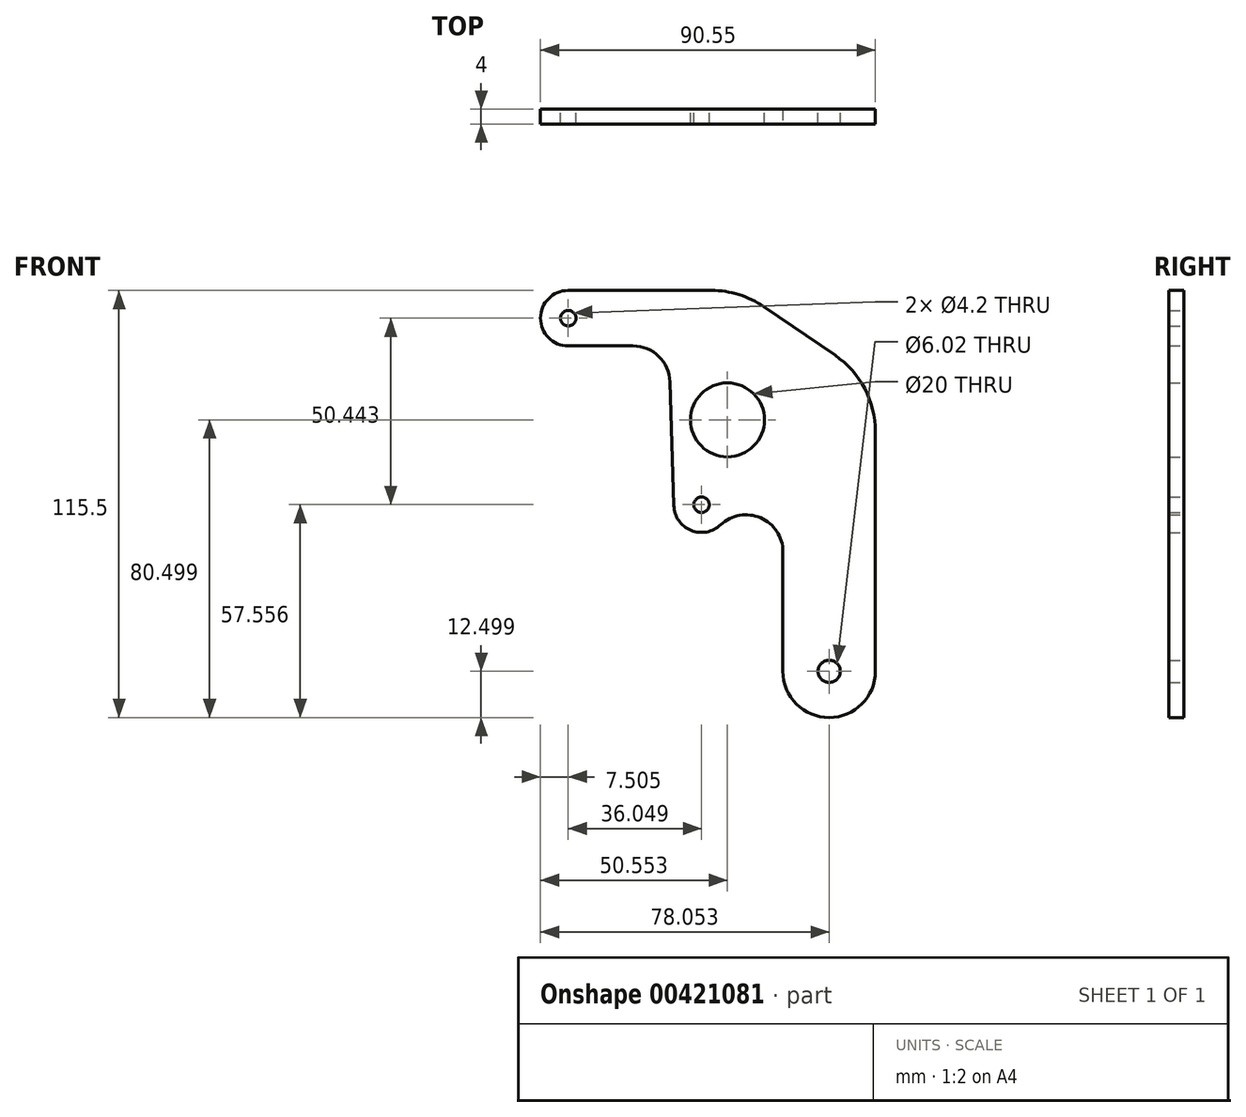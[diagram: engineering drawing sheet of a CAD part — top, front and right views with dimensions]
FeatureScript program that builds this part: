
annotation { "Feature Type Name" : "Feature", "Feature Type Description" : "" }
export const myFeature = defineFeature(function(context is Context, id is Id, definition is map)
    precondition{}
    {
        {
            var Q0;
            Q0=qCreatedBy(makeId("Front.planeOp"),FACE);
            var sketch = newSketch(context, id + "F0", { "sketchPlane" : qUnion([Q0])});
            skLineSegment(sketch, "E0", {"start": v(17.8, -32.82) * mm, "end": v(17.8, 31.99) * mm});
            skLineSegment(sketch, "E1", {"start": v(6.91, 52.62) * mm, "end": v(-12.39, 65.82) * mm});
            skLineSegment(sketch, "E2", {"start": v(-26.5, 70.18) * mm, "end": v(-65.25, 70.18) * mm});
            skLineSegment(sketch, "E3", {"start": v(-65.25, 55.18) * mm, "end": v(-47.72, 55.18) * mm});
            skLineSegment(sketch, "E4", {"start": v(-7.2, 25.92) * mm, "end": v(-7.2, -32.82) * mm});
            skLineSegment(sketch, "E5", {"start": v(-23.76, 7.07) * mm, "end": v(-6.5, 25.25) * mm});
            skLineSegment(sketch, "E6.trimOffspring", {"start": v(-7.2, 25.92) * mm, "end": v(-6.5, 25.25) * mm});
            skCircle(sketch, "E7", {"center": v(-29.2, 12.24) * mm, "radius": 2.1 * mm});
            skCircle(sketch, "E8", {"center": v(-65.25, 62.68) * mm, "radius": 2.1 * mm});
            skCircle(sketch, "E9", {"center": v(5.3, -32.82) * mm, "radius": 3.01 * mm});
            skCircle(sketch, "E10", {"center": v(-22.2, 35.18) * mm, "radius": 10 * mm});
            skArc(sketch, "E11", {"start": v(-36.7, 12) * mm, "mid": v(-31.87, 5.23) * mm, "end": v(-23.76, 7.07) * mm});
            skArc(sketch, "E12", {"start": v(-65.25, 70.18) * mm, "mid": v(-72.75, 62.68) * mm, "end": v(-65.25, 55.18) * mm});
            skArc(sketch, "E13", {"start": v(-7.2, -32.82) * mm, "mid": v(5.3, -45.32) * mm, "end": v(17.8, -32.82) * mm});
            skLineSegment(sketch, "E14.trimOffspring", {"start": v(-27.67, 4.9) * mm, "end": v(-26.47, 4.21) * mm});
            skPoint(sketch, "E15.orphan", {"position": v(17.8, -42.82) * mm});
            skPoint(sketch, "E16.orphan", {"position": v(-7.2, -42.82) * mm});
            skLineSegment(sketch, "E17", {"start": v(-37.72, 45.49) * mm, "end": v(-36.7, 12) * mm});
            skPoint(sketch, "E18.orphan", {"position": v(-36.32, 0) * mm});
            skPoint(sketch, "E19.visualSharp", {"position": v(-18.77, 70.18) * mm});
            skArc(sketch, "E19.filletArc", {"start": v(-12.39, 65.82) * mm, "mid": v(-19.11, 69.06) * mm, "end": v(-26.5, 70.18) * mm});
            skPoint(sketch, "E20.visualSharp", {"position": v(17.8, 45.18) * mm});
            skArc(sketch, "E20.filletArc", {"start": v(17.8, 31.99) * mm, "mid": v(14.91, 43.65) * mm, "end": v(6.91, 52.62) * mm});
            skPoint(sketch, "E21.visualSharp", {"position": v(-38.02, 55.18) * mm});
            skArc(sketch, "E21.filletArc", {"start": v(-37.72, 45.49) * mm, "mid": v(-40.76, 52.36) * mm, "end": v(-47.72, 55.18) * mm});
            skSolve(sketch);
        }
        {
            var Q0;
            Q0 = qSketchRegion(id + "F0", true);
            extrude(context, id + "F1", {"entities" : qUnion([Q0]), "depth" : 4 * mm});
        }
        {
            var Q0;
            Q0=makeQuery(id+"F1.opExtrude","SWEPT_EDGE",EDGE,{"disambiguationData":[OSD([sQuery(id+"F0.wireOp",EDGE,"E4"),sQuery(id+"F0.wireOp",EDGE,"E5")])]});
            fillet(context, id + "F2", {"entities" : qUnion([Q0]), "radius" : 10 * mm, "tangentPropagation" : true, "allowEdgeOverflow" : false});
        }
    });
